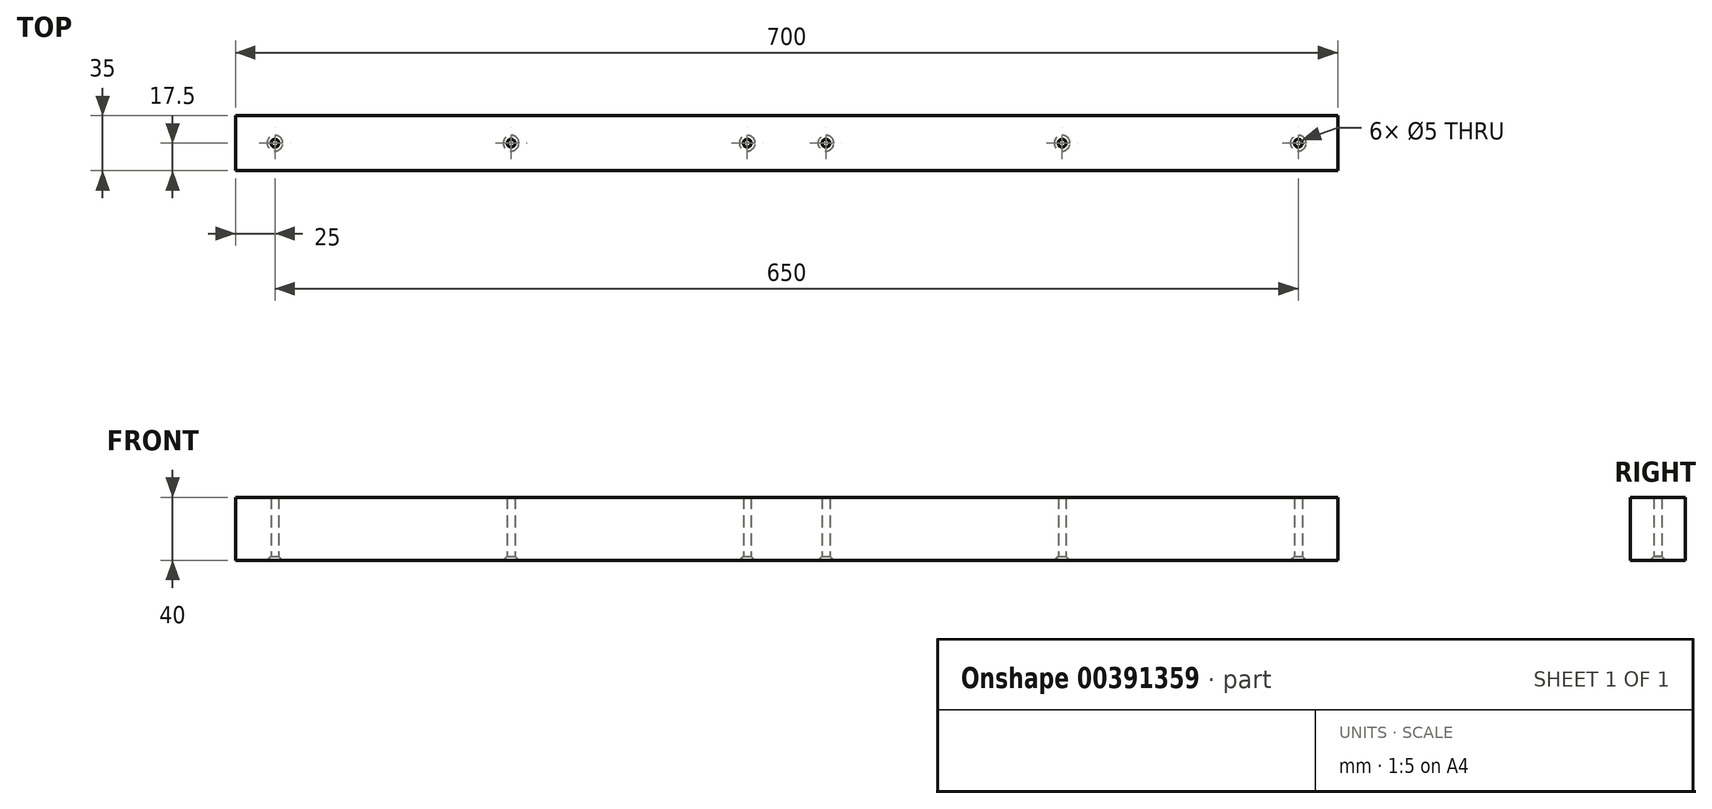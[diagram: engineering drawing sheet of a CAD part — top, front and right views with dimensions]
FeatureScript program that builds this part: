
annotation { "Feature Type Name" : "Feature", "Feature Type Description" : "" }
export const myFeature = defineFeature(function(context is Context, id is Id, definition is map)
    precondition{}
    {
        {
            var Q0;
            Q0=qCreatedBy(makeId("Right.planeOp"),FACE);
            var sketch = newSketch(context, id + "F0", { "sketchPlane" : qUnion([Q0])});
            skLineSegment(sketch, "E0.bottom", {"start": v(35, 47.25) * mm, "end": v(0, 47.25) * mm});
            skLineSegment(sketch, "E0.top", {"start": v(35, 7.25) * mm, "end": v(0, 7.25) * mm});
            skLineSegment(sketch, "E0.left", {"start": v(35, 47.25) * mm, "end": v(35, 7.25) * mm});
            skLineSegment(sketch, "E0.right", {"start": v(0, 47.25) * mm, "end": v(0, 7.25) * mm});
            skSolve(sketch);
        }
        {
            var Q0;
            Q0 = qSketchRegion(id + "F0", true);
            extrude(context, id + "F1", {"entities" : qUnion([Q0]), "depth" : 700 * mm});
        }
        {
            var Q0;
            Q0=makeQuery(id+"F1.opExtrude","SWEPT_FACE",FACE,{"disambiguationData":[OSD([sQuery(id+"F0.wireOp",EDGE,"E0.top")])]});
            var sketch = newSketch(context, id + "F2", { "sketchPlane" : qUnion([Q0])});
            skLineSegment(sketch, "E1", {"start": v(0, -17.5) * mm, "end": v(700, -17.5) * mm, "construction": true});
            skPoint(sketch, "E2", {"position": v(25, -17.5) * mm});
            skPoint(sketch, "E3", {"position": v(675, -17.5) * mm});
            skPoint(sketch, "E4", {"position": v(175, -17.5) * mm});
            skPoint(sketch, "E5", {"position": v(525, -17.5) * mm});
            skPoint(sketch, "E6", {"position": v(325, -17.5) * mm});
            skPoint(sketch, "E7", {"position": v(375, -17.5) * mm});
            skSolve(sketch);
        }
        {
            var Q0;
            Q0=sQuery(id+"F2.wireOp",VERTEX,"E2");
            var Q1;
            Q1=sQuery(id+"F2.wireOp",VERTEX,"E4");
            var Q2;
            Q2=sQuery(id+"F2.wireOp",VERTEX,"E6");
            var Q3;
            Q3=sQuery(id+"F2.wireOp",VERTEX,"E7");
            var Q4;
            Q4=sQuery(id+"F2.wireOp",VERTEX,"E3");
            var Q5;
            Q5=sQuery(id+"F2.wireOp",VERTEX,"E5");
            var Q6;
            Q6=makeQuery(id+"F1.opExtrude","SWEPT_BODY",BODY,{"disambiguationData":[OSD([sQuery(id+"F0.wireOp",EDGE,"E0.bottom"),sQuery(id+"F0.wireOp",EDGE,"E0.top"),sQuery(id+"F0.wireOp",EDGE,"E0.left"),sQuery(id+"F0.wireOp",EDGE,"E0.right")])]});
            hole(context, id + "F3", {"style" : HoleStyle.C_SINK, "endStyle" : HoleEndStyle.THROUGH, "holeDiameter" : 5 * mm, "cSinkDiameter" : 10 * mm, "cSinkAngle" : 90 * degree, "isTappedThrough" : true, "tappedDepth" : 12 * mm, "tapClearance" : 3, "startFromSketch" : true, "locations" : qUnion([Q0, Q1, Q2, Q3, Q4, Q5]), "scope" : qUnion([Q6])});
        }
    });
